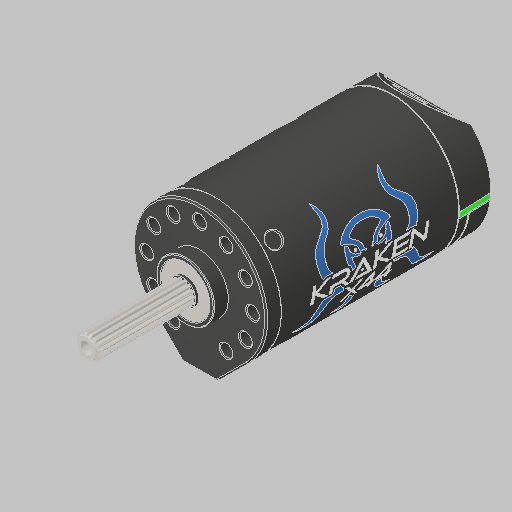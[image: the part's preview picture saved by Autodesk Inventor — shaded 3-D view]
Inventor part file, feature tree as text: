
AUTODESK INVENTOR PART (.ipt)
format: ipt  version: 2023.5 (Build 275446000, 446)  size: 6,384,128 bytes
history: native  units: in
note: dims shown in document units (in); Inventor stores cm internally (conversion verified against a paired STEP export)
features: chamfer x1, boolean_combine x1
ambient origin geometry x8: Origin, YZ Plane, XZ Plane, XY Plane, X Axis, Y Axis, Z Axis, Center Point
bodies: Solid1 (feature_tree), Solid2 (feature_tree)
feature tree (2):
  chamfer  "Chamfer5"  [1 undecoded]
  boolean_combine  "Combine5"
note: 1 required parameter value undecoded (feature->parameter linkage not recoverable at this tier; creation-order binding heuristic only, values carry confidence <= 0.55)
